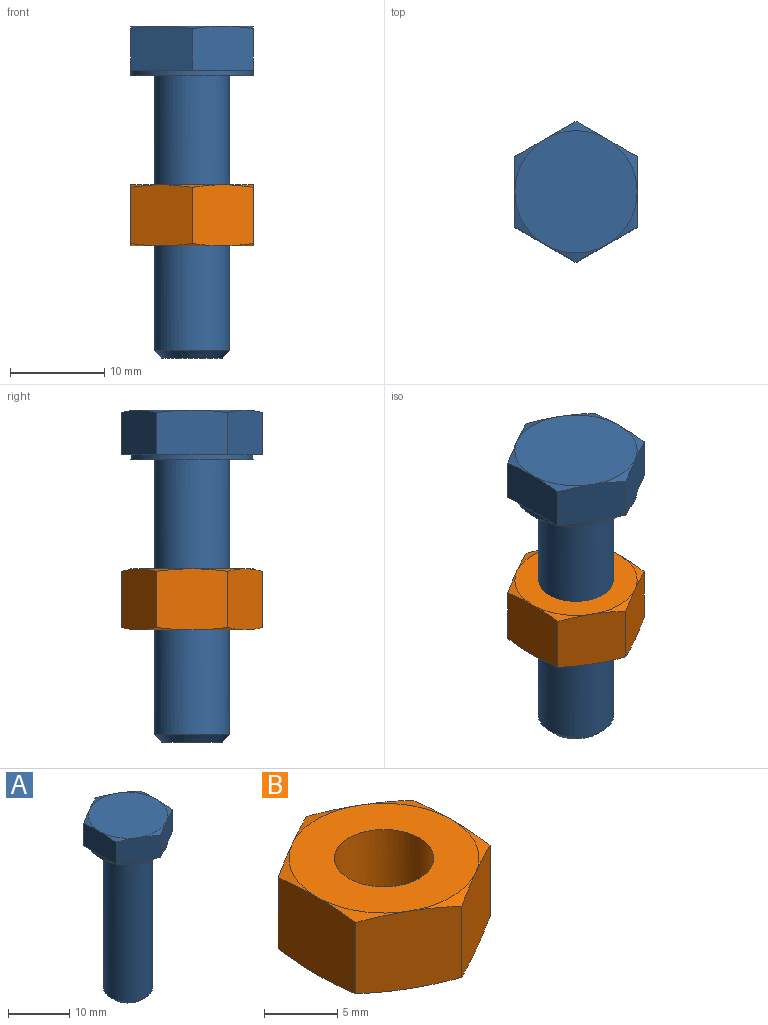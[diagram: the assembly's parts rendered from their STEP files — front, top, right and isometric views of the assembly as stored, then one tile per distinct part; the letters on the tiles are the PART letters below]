
ASSEMBLY  parts=2 mates=1
PART A: 24 faces, bbox 15.6x15.6x35.9 mm
  f0: plane 7.06x5.26mm, normal (-0.5,0.87,0), area 34.6mm2, adj f2,f5,f10,f15,f17,f23
  f1: plane 8.07x5.26mm, normal (1,0,0), area 34.6mm2, adj f4,f5,f11,f12,f18,f22
  f2: plane 8.07x5.26mm, normal (-1,0,0), area 34.6mm2, adj f0,f3,f14,f15,f19,f23
  f3: plane 7.06x5.26mm, normal (-0.5,-0.87,0), area 34.6mm2, adj f2,f4,f13,f14,f19,f21
  f4: plane 7.06x5.26mm, normal (0.5,-0.87,0), area 34.6mm2, adj f1,f3,f12,f13,f18,f21
  f5: plane 7.06x5.26mm, normal (0.5,0.87,0), area 34.6mm2, adj f0,f1,f10,f11,f17,f22
  f6: plane 13x13mm, normal (0,0,-1), area 82.5mm2, adj f8,f20
  f7: plane 6.4x6.4mm, normal (0,0,-1), area 32.2mm2, adj f9
  f8: cylinder r=4mm len=29.2mm, axis (0,0,1), area 733.9mm2, adj f6,f9
  f9: cone r=4mm half-angle=45deg, axis (0,0,1), area 25.6mm2, adj f7,f8
  f10: cone r=6.5mm half-angle=75deg, axis (0,0,-1), area 3.7mm2, adj f0,f5,f16
  f11: cone r=6.5mm half-angle=75deg, axis (0,0,-1), area 3.7mm2, adj f1,f5,f16
  f12: cone r=6.5mm half-angle=75deg, axis (0,0,-1), area 3.7mm2, adj f1,f4,f16
  f13: cone r=6.5mm half-angle=75deg, axis (0,0,-1), area 3.7mm2, adj f3,f4,f16
  f14: cone r=6.5mm half-angle=75deg, axis (0,0,-1), area 3.7mm2, adj f2,f3,f16
  f15: cone r=6.5mm half-angle=75deg, axis (0,0,-1), area 3.7mm2, adj f0,f2,f16
  f16: plane 13x13mm, normal (0,0,1), area 132.7mm2, adj f10,f11,f12,f13,f14,f15
  f17: plane 6.5x1.88mm, normal (0,0,-1), area 2.3mm2, adj f0,f5,f20
  f18: plane 5.63x3.25mm, normal (0,0,-1), area 2.3mm2, adj f1,f4,f20
  f19: plane 5.63x3.25mm, normal (0,0,-1), area 2.3mm2, adj f2,f3,f20
  f20: cylinder r=6.5mm len=13mm, axis (0,0,-1), area 24.5mm2, adj f6,f17,f18,f19,f21,f22,f23
  f21: plane 6.5x1.88mm, normal (0,0,-1), area 2.3mm2, adj f3,f4,f20
  f22: plane 5.63x3.25mm, normal (0,0,-1), area 2.3mm2, adj f1,f5,f20
  f23: plane 5.63x3.25mm, normal (0,0,-1), area 2.3mm2, adj f0,f2,f20
PART B: 21 faces, bbox 15.6x15.6x7.1 mm
  f0: plane 13x13mm, normal (0,0,1), area 96.4mm2, adj f8,f15,f16,f17,f18,f19,f20
  f1: plane 13x13mm, normal (0,0,-1), area 96.4mm2, adj f8,f9,f10,f11,f12,f13,f14
  f2: plane 7.06x7.06mm, normal (-0.5,0.87,0), area 47.4mm2, adj f3,f7,f9,f14,f16,f20
  f3: plane 8.07x7.06mm, normal (-1,0,0), area 47.4mm2, adj f2,f4,f13,f14,f19,f20
  f4: plane 7.06x7.06mm, normal (-0.5,-0.87,0), area 47.4mm2, adj f3,f5,f12,f13,f18,f19
  f5: plane 7.06x7.06mm, normal (0.5,-0.87,0), area 47.4mm2, adj f4,f6,f11,f12,f17,f18
  f6: plane 8.07x7.06mm, normal (1,0,0), area 47.4mm2, adj f5,f7,f10,f11,f15,f17
  f7: plane 7.06x7.06mm, normal (0.5,0.87,0), area 47.4mm2, adj f2,f6,f9,f10,f15,f16
  f8: cylinder r=3.4mm len=6.8mm, axis (0,0,-1), area 138.9mm2, adj f0,f1
  f9: cone r=6.5mm half-angle=75deg, axis (0,0,1), area 3.7mm2, adj f1,f2,f7
  f10: cone r=6.5mm half-angle=75deg, axis (0,0,1), area 3.7mm2, adj f1,f6,f7
  f11: cone r=6.5mm half-angle=75deg, axis (0,0,1), area 3.7mm2, adj f1,f5,f6
  f12: cone r=6.5mm half-angle=75deg, axis (0,0,1), area 3.7mm2, adj f1,f4,f5
  f13: cone r=6.5mm half-angle=75deg, axis (0,0,1), area 3.7mm2, adj f1,f3,f4
  f14: cone r=6.5mm half-angle=75deg, axis (0,0,1), area 3.7mm2, adj f1,f2,f3
  f15: cone r=18.63mm half-angle=75deg, axis (0,0,-1), area 3.7mm2, adj f0,f6,f7
  f16: cone r=18.63mm half-angle=75deg, axis (0,0,-1), area 3.7mm2, adj f0,f2,f7
  f17: cone r=18.63mm half-angle=75deg, axis (0,0,-1), area 3.7mm2, adj f0,f5,f6
  f18: cone r=18.63mm half-angle=75deg, axis (0,0,-1), area 3.7mm2, adj f0,f4,f5
  f19: cone r=18.63mm half-angle=75deg, axis (0,0,-1), area 3.7mm2, adj f0,f3,f4
  f20: cone r=18.63mm half-angle=75deg, axis (0,0,-1), area 3.7mm2, adj f0,f2,f3
PLACE A at identity
PLACE B rot(axis=(0,0,1),180deg) t=(0,0,-18.09)mm
MATE slider A.f8 <-> B.f8  axis (0,0,-1) through (0,0,0)mm
